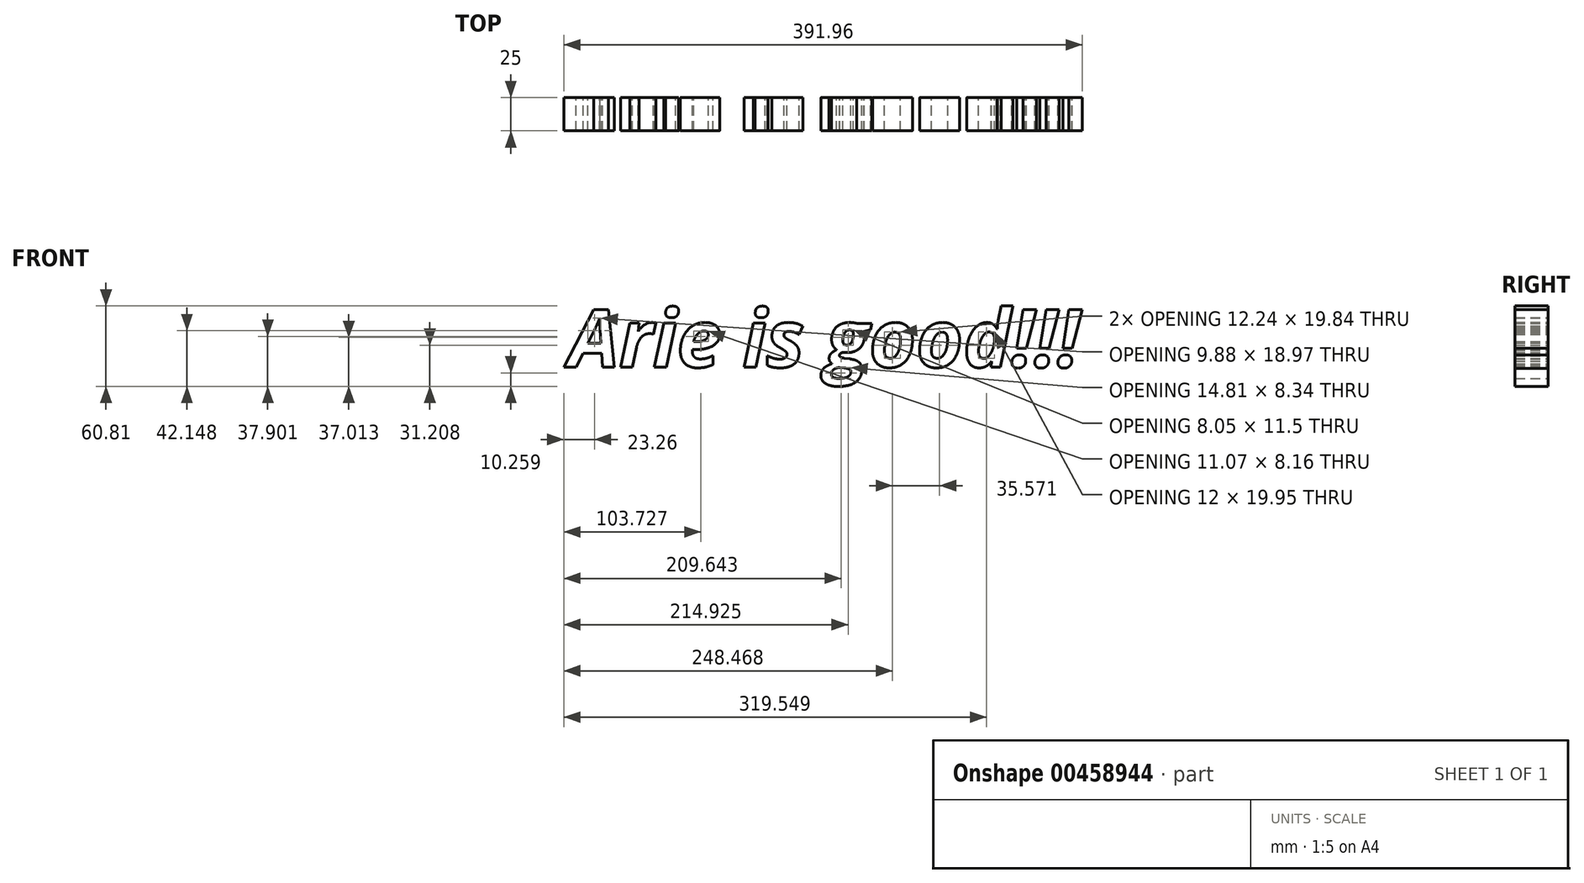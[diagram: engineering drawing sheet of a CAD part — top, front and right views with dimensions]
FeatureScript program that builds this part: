
annotation { "Feature Type Name" : "Feature", "Feature Type Description" : "" }
export const myFeature = defineFeature(function(context is Context, id is Id, definition is map)
    precondition{}
    {
        {
            var Q0;
            Q0=qCreatedBy(makeId("Front.planeOp"),FACE);
            var sketch = newSketch(context, id + "F0", { "sketchPlane" : qUnion([Q0])});
            skText(sketch, "E0", { "text": "Arie is good!!!", "fontName": "OpenSans-BoldItalic.ttf"});
            const initialGuessF0  = {"E0": [-0.03497, -0.01872, 1, 0, 0.04378]};
            skSetInitialGuess(sketch, initialGuessF0);
            skSolve(sketch);
        }
        {
            var Q0;
            Q0 = qSketchRegion(id + "F0", true);
            extrude(context, id + "F1", {"entities" : qUnion([Q0]), "depth" : 25 * mm});
        }
    });
